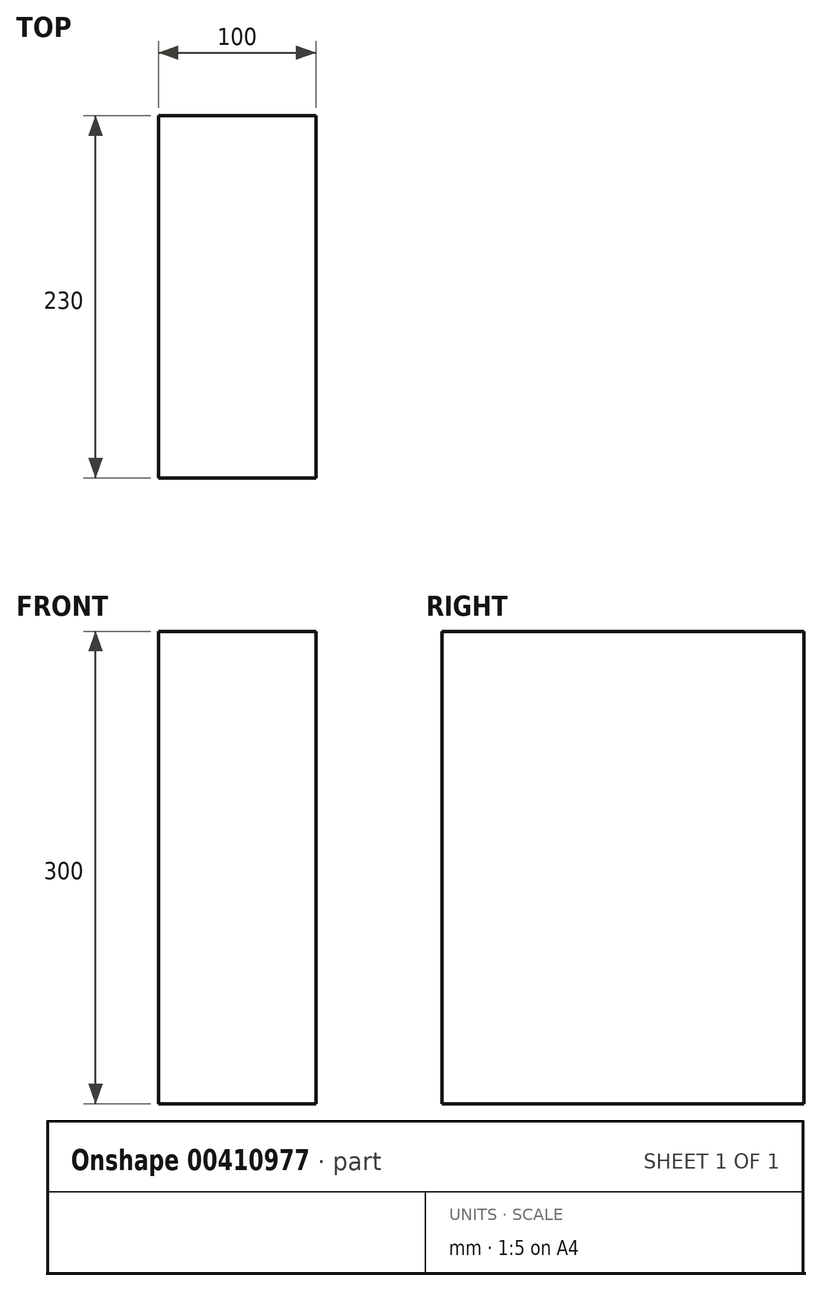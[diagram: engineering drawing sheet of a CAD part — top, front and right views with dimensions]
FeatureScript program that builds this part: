
annotation { "Feature Type Name" : "Feature", "Feature Type Description" : "" }
export const myFeature = defineFeature(function(context is Context, id is Id, definition is map)
    precondition{}
    {
        {
            var Q0;
            Q0=qCreatedBy(makeId("Top.planeOp"),FACE);
            var sketch = newSketch(context, id + "F0", { "sketchPlane" : qUnion([Q0])});
            skLineSegment(sketch, "E0.bottom", {"start": v(0, 0) * mm, "end": v(100, 0) * mm});
            skLineSegment(sketch, "E0.top", {"start": v(0, 230) * mm, "end": v(100, 230) * mm});
            skLineSegment(sketch, "E0.left", {"start": v(0, 0) * mm, "end": v(0, 230) * mm});
            skLineSegment(sketch, "E0.right", {"start": v(100, 0) * mm, "end": v(100, 230) * mm});
            skSolve(sketch);
        }
        {
            var Q0;
            Q0=makeQuery(id+"F0.imprint","IMPRINT",FACE,{"disambiguationData":[TD([[makeQuery(id+"F0.imprint","IMPRINT",EDGE,{"derivedFrom":sQuery(id+"F0.wireOp",EDGE,"E0.bottom")}),1.0]])]});
            extrude(context, id + "F1", {"entities" : qUnion([Q0]), "depth" : 300 * mm});
        }
    });
